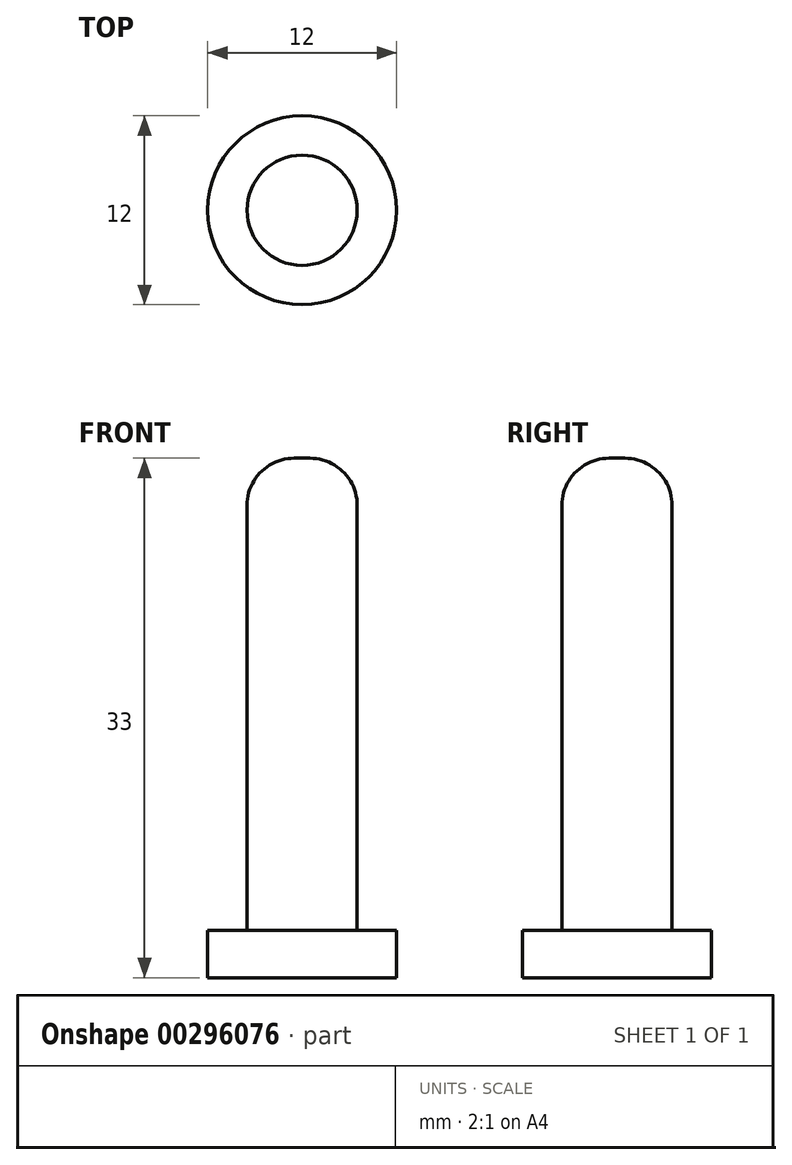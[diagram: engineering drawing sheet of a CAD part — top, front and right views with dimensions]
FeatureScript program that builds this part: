
annotation { "Feature Type Name" : "Feature", "Feature Type Description" : "" }
export const myFeature = defineFeature(function(context is Context, id is Id, definition is map)
    precondition{}
    {
        {
            var Q0;
            Q0=qCreatedBy(makeId("Top.planeOp"),FACE);
            var sketch = newSketch(context, id + "F0", { "sketchPlane" : qUnion([Q0])});
            skCircle(sketch, "E0", {"center": v(0, 0) * mm, "radius": 6 * mm});
            skSolve(sketch);
        }
        {
            var Q0;
            Q0 = qSketchRegion(id + "F0", true);
            extrude(context, id + "F1", {"entities" : qUnion([Q0]), "depth" : 3 * mm});
        }
        {
            var Q0;
            Q0=makeQuery(id+"F1.opExtrude","CAP_FACE",FACE,{"disambiguationData":[OSD([sQuery(id+"F0.wireOp",EDGE,"E0")])],"isStart":false});
            var sketch = newSketch(context, id + "F2", { "sketchPlane" : qUnion([Q0])});
            skCircle(sketch, "E1", {"center": v(0, 0) * mm, "radius": 3.5 * mm});
            skSolve(sketch);
        }
        {
            var Q0;
            Q0=makeQuery(id+"F2.imprint","IMPRINT",FACE,{"disambiguationData":[TD([[makeQuery(id+"F2.imprint","IMPRINT",EDGE,{"derivedFrom":sQuery(id+"F2.wireOp",EDGE,"E1")}),1.0]])]});
            extrude(context, id + "F3", {"entities" : qUnion([Q0]), "operationType" : NewBodyOperationType.ADD, "depth" : 30 * mm});
        }
        {
            var Q0;
            Q0=makeQuery(id+"F3.opExtrude","CAP_EDGE",EDGE,{"disambiguationData":[OSD([sQuery(id+"F2.wireOp",EDGE,"E1")])],"isStart":true});
            var Q1;
            Q1=makeQuery(id+"F3.opExtrude","CAP_EDGE",EDGE,{"disambiguationData":[OSD([sQuery(id+"F2.wireOp",EDGE,"E1")])],"isStart":false});
            fillet(context, id + "F4", {"entities" : qUnion([Q0, Q1]), "radius" : 3 * mm, "tangentPropagation" : true, "allowEdgeOverflow" : false});
        }
    });
